# Revit family: Backwaren-Kühltische400x600 - Zentral
name_source: partatom
category: Sonderausstattung
revit_build: Autodesk Revit 2015 (Build: 20160512_1515(x64)
units: mm (PartAtom-declared; Revit-internal decimal feet)

## types (2) — shared parameters
Abstand Display seitlich = 10 mm  [stored 0.0328084 ft]
Abstand Leitungen = 100 mm  [stored 0.328084 ft]
Abstand Logo = 265 mm
Aufkantung Höhe = 50 mm  [stored 0.164042 ft]
Aufkantung Stärke = 6 mm  [stored 0.019685 ft]
DN Flüssigkeitsleitung = 6 mm  [stored 0.019685 ft]
DN Saugleitung = 8 mm  [stored 0.0262467 ft]
DN Trichterablauf = 50 mm  [stored 0.164042 ft]
Höhe Elektroanschluss = 150 mm
Höhe Leitungsanschluss = 500 mm  [stored 1.64042 ft]
Korpus Höhe = 650 mm  [stored 2.13255 ft]
Korpus Tiefe = 720 mm
Kältemittel = R134a
Material = Edelstahl AISI 304
Pfosten 1 = Ja
Pfosten Abstand = 515 mm
Pfosten Breite = 100 mm  [stored 0.328084 ft]
Pfosten Tiefe = 50 mm  [stored 0.164042 ft]
Platte Tiefe = 800 mm  [stored 2.62467 ft]
Pole = 1
Rückwand Stärke = 50 mm  [stored 0.164042 ft]
Scheinleistung = 0 VA
Seitenteil Breite = 220 mm  [stored 0.721785 ft]
Seitenteilwand Stärke = 15 mm  [stored 0.0492126 ft]
Seitenwand Stärke = 50 mm  [stored 0.164042 ft]
Sockelhöhe = 150 mm
Spannung = 230 V
Temp. Bereich = -2°C / +10°C
Tür_1 = Ja
Tür_2 = Ja
Türen Breite = 495 mm  [stored 1.62402 ft]
Türen Breite halb = 248 mm
Türen Höhe = 630 mm  [stored 2.06693 ft]
Türen Lücke = 40 mm  [stored 0.131234 ft]
Türen Stärke = 50 mm  [stored 0.164042 ft]
Wand oben Stärke = 50 mm  [stored 0.164042 ft]
Wand unten Stärke = 50 mm  [stored 0.164042 ft]
Öffnungstiefe = 570 mm

## per-type parameters (varying)
| type | Artnr mit Platte | Artnr mit Platte und Aufkantung | Artnr ohne Platte | Breite | Kapazität | Korpus Breite | Kälteleistung | Marmorplatte Material | Pfosten 2 | Pfosten Anzahl | Tür_3 | Türen Anzahl | Versatz Tür zu Seitenteil | Watt |
| 650x1300 2-türig | KTO 824662 | KTO 824661 | KTO 824660 | 1300 mm | 2 x 10 x EN6040 | 1065 mm | 310 Watt -15°C VT | <Nach Kategorie> | Nein | 1 | Nein | 2 | 20 mm  [stored 0.0656168 ft] | 80 W |
| 650x1845 3-türig | KTO 834662 | KTO 834661 | KTO 834660 | 1845 mm | 3 x 10 x EN6040 | 1610 mm | 430 Watt -15°C VT | Marmor | Ja | 2 | Ja | 3 | 30 mm  [stored 0.0984252 ft] | 130 W |

note: [stored X ft] marks values corroborated as IEEE doubles in the binary element streams (Revit-internal decimal feet)

## geometry (parser evidence)
native form markers: Blend x13, Sweep x6
no freeform markers — native parametric forms only
